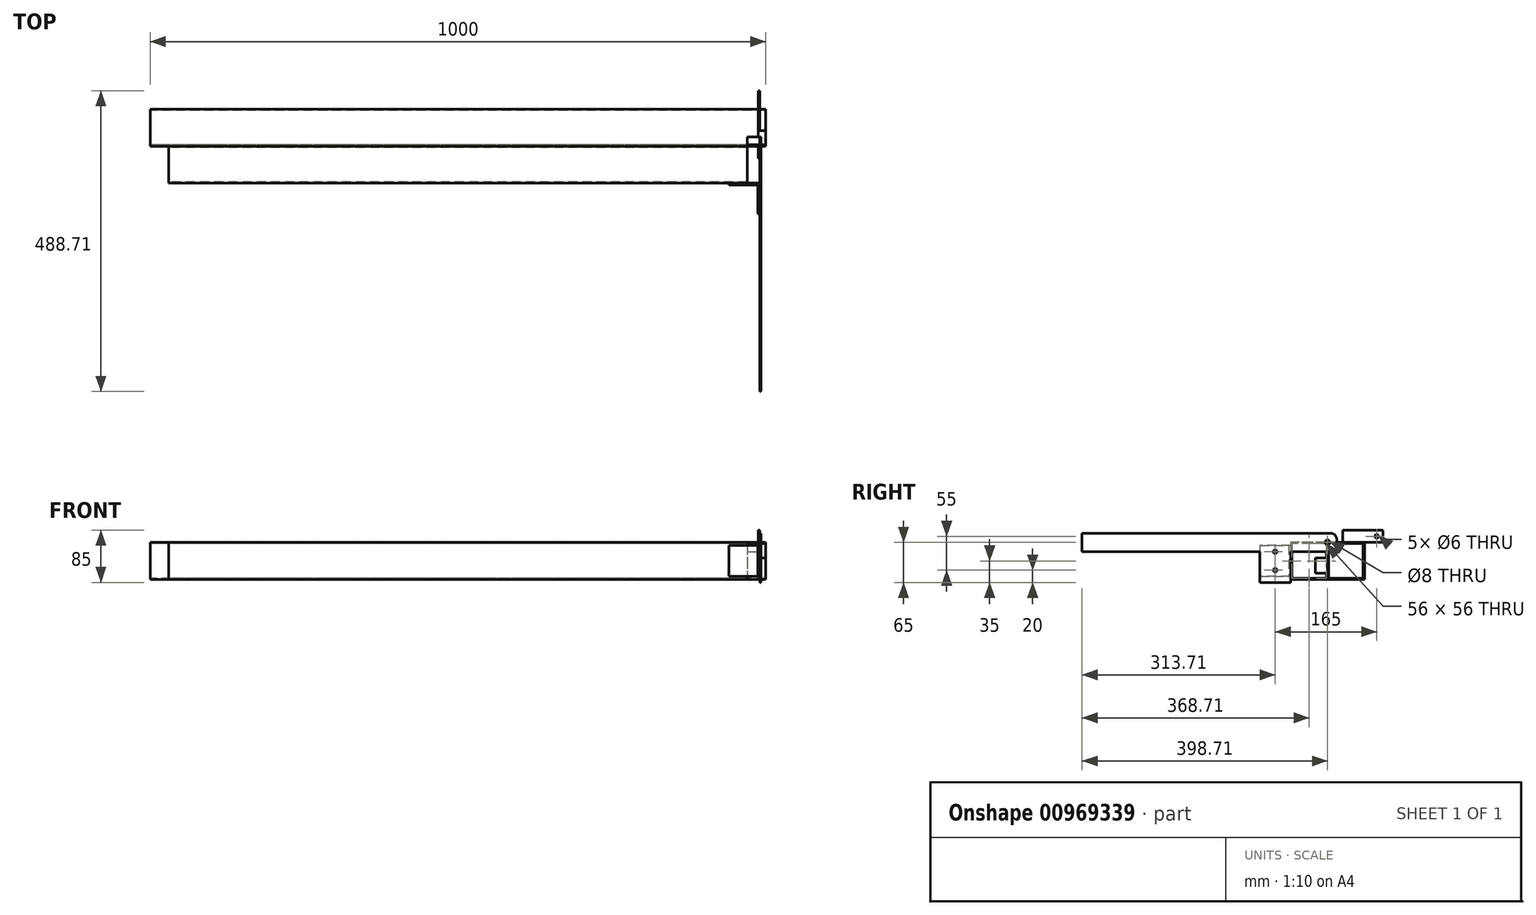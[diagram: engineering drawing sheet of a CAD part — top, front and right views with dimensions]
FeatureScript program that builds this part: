
annotation { "Feature Type Name" : "Feature", "Feature Type Description" : "" }
export const myFeature = defineFeature(function(context is Context, id is Id, definition is map)
    precondition{}
    {
        {
            var Q0;
            Q0=qCreatedBy(makeId("Right.planeOp"),FACE);
            var sketch = newSketch(context, id + "F0", { "sketchPlane" : qUnion([Q0])});
            skLineSegment(sketch, "E0.bottom", {"start": v(30, 30) * mm, "end": v(-30, 30) * mm});
            skLineSegment(sketch, "E0.top", {"start": v(30, -30) * mm, "end": v(-30, -30) * mm});
            skLineSegment(sketch, "E0.left", {"start": v(30, 30) * mm, "end": v(30, -30) * mm});
            skLineSegment(sketch, "E0.right", {"start": v(-30, 30) * mm, "end": v(-30, -30) * mm});
            skPoint(sketch, "E0.middle", {"position": v(0, 0) * mm});
            skLineSegment(sketch, "E1.bottom", {"start": v(28, 28) * mm, "end": v(-28, 28) * mm});
            skLineSegment(sketch, "E1.top", {"start": v(28, -28) * mm, "end": v(-28, -28) * mm});
            skLineSegment(sketch, "E1.left", {"start": v(28, 28) * mm, "end": v(28, -28) * mm});
            skLineSegment(sketch, "E1.right", {"start": v(-28, 28) * mm, "end": v(-28, -28) * mm});
            skSolve(sketch);
        }
        {
            var Q0;
            Q0=makeQuery(id+"F0.imprint","IMPRINT",FACE,{"disambiguationData":[TD([[makeQuery(id+"F0.imprint","IMPRINT",EDGE,{"derivedFrom":sQuery(id+"F0.wireOp",EDGE,"E0.bottom")}),1.0]])]});
            extrude(context, id + "F1", {"entities" : qUnion([Q0]), "depth" : 500 * mm, "offsetDistance" : 25 * mm, "hasSecondDirection" : true, "secondDirectionOppositeDirection" : true, "secondDirectionDepth" : 500 * mm});
        }
        {
            var Q0;
            Q0=qCreatedBy(makeId("Right.planeOp"),FACE);
            cPlane(context, id + "F2", {"entities" : qUnion([Q0]), "cplaneType" : CPlaneType.OFFSET, "offset" : 490 * mm, "width" : 150 * mm, "height" : 150 * mm});
        }
        {
            var Q0;
            Q0=qCreatedBy(id+"F2.planeOp",FACE);
            var sketch = newSketch(context, id + "F3", { "sketchPlane" : qUnion([Q0])});
            skLineSegment(sketch, "E2", {"start": v(-50, 50) * mm, "end": v(60, 50) * mm});
            skLineSegment(sketch, "E3", {"start": v(60, 50) * mm, "end": v(60, 30) * mm});
            skLineSegment(sketch, "E4", {"start": v(60, 30) * mm, "end": v(-10, 30) * mm});
            skLineSegment(sketch, "E5", {"start": v(-10, 30) * mm, "end": v(-10, 10) * mm});
            skLineSegment(sketch, "E6", {"start": v(-10, 10) * mm, "end": v(-30, 10) * mm});
            skLineSegment(sketch, "E7", {"start": v(-30, 10) * mm, "end": v(-30, -20) * mm});
            skLineSegment(sketch, "E8", {"start": v(-30, -20) * mm, "end": v(-50, -20) * mm});
            skLineSegment(sketch, "E9", {"start": v(-50, -20) * mm, "end": v(-50, 50) * mm});
            skCircle(sketch, "E10", {"center": v(-30, 30) * mm, "radius": 4 * mm});
            skCircle(sketch, "E11", {"center": v(50, 40) * mm, "radius": 3 * mm});
            skSolve(sketch);
        }
        {
            var Q0;
            Q0=makeQuery(id+"F3.imprint","IMPRINT",FACE,{"disambiguationData":[TD([[makeQuery(id+"F3.imprint","IMPRINT",EDGE,{"derivedFrom":sQuery(id+"F3.wireOp",EDGE,"E2")}),-1.0]])]});
            extrude(context, id + "F4", {"entities" : qUnion([Q0]), "oppositeDirection" : true, "depth" : 2 * mm, "offsetDistance" : 25 * mm});
        }
        {
            var Q0;
            Q0=makeQuery(id+"F1.opExtrude","CAP_FACE",FACE,{"disambiguationData":[OSD([sQuery(id+"F0.wireOp",EDGE,"E0.bottom"),sQuery(id+"F0.wireOp",EDGE,"E0.top"),sQuery(id+"F0.wireOp",EDGE,"E0.left"),sQuery(id+"F0.wireOp",EDGE,"E0.right"),sQuery(id+"F0.wireOp",EDGE,"E1.bottom"),sQuery(id+"F0.wireOp",EDGE,"E1.top"),sQuery(id+"F0.wireOp",EDGE,"E1.left"),sQuery(id+"F0.wireOp",EDGE,"E1.right")])],"isStart":false});
            cPlane(context, id + "F5", {"entities" : qUnion([Q0]), "cplaneType" : CPlaneType.OFFSET, "offset" : 30 * mm, "oppositeDirection" : true, "width" : 150 * mm, "height" : 150 * mm});
        }
        {
            var Q0;
            Q0=makeQuery(id+"F1.opExtrude","CAP_FACE",FACE,{"disambiguationData":[OSD([sQuery(id+"F0.wireOp",EDGE,"E0.bottom"),sQuery(id+"F0.wireOp",EDGE,"E0.top"),sQuery(id+"F0.wireOp",EDGE,"E0.left"),sQuery(id+"F0.wireOp",EDGE,"E0.right"),sQuery(id+"F0.wireOp",EDGE,"E1.bottom"),sQuery(id+"F0.wireOp",EDGE,"E1.top"),sQuery(id+"F0.wireOp",EDGE,"E1.left"),sQuery(id+"F0.wireOp",EDGE,"E1.right")])],"isStart":false});
            cPlane(context, id + "F6", {"entities" : qUnion([Q0]), "cplaneType" : CPlaneType.OFFSET, "offset" : 12 * mm, "oppositeDirection" : true, "width" : 150 * mm, "height" : 150 * mm});
        }
        {
            var Q0;
            Q0=qCreatedBy(id+"F5.planeOp",FACE);
            var sketch = newSketch(context, id + "F7", { "sketchPlane" : qUnion([Q0])});
            skLineSegment(sketch, "E12.bottom", {"start": v(-35.72, 35.11) * mm, "end": v(-15, 35.11) * mm});
            skLineSegment(sketch, "E12.top", {"start": v(-35.72, 15) * mm, "end": v(-15, 15) * mm});
            skLineSegment(sketch, "E12.left", {"start": v(-35.72, 35.11) * mm, "end": v(-35.72, 15) * mm});
            skLineSegment(sketch, "E12.right", {"start": v(-15, 35.11) * mm, "end": v(-15, 15) * mm});
            skSolve(sketch);
        }
        {
            var Q0;
            Q0=makeQuery(id+"F7.imprint","IMPRINT",FACE,{"disambiguationData":[TD([[makeQuery(id+"F7.imprint","IMPRINT",EDGE,{"derivedFrom":sQuery(id+"F7.wireOp",EDGE,"E12.bottom")}),-1.0]])]});
            extrude(context, id + "F8", {"entities" : qUnion([Q0]), "operationType" : NewBodyOperationType.REMOVE, "depth" : 100 * mm, "offsetDistance" : 25 * mm});
        }
        {
            var Q0;
            Q0=qCreatedBy(id+"F6.planeOp",FACE);
            var sketch = newSketch(context, id + "F9", { "sketchPlane" : qUnion([Q0])});
            skLineSegment(sketch, "E13.bottom", {"start": v(-60.98, 60.55) * mm, "end": v(-5, 60.55) * mm});
            skLineSegment(sketch, "E13.top", {"start": v(-60.98, 5) * mm, "end": v(-5, 5) * mm});
            skLineSegment(sketch, "E13.left", {"start": v(-60.98, 60.55) * mm, "end": v(-60.98, 5) * mm});
            skLineSegment(sketch, "E13.right", {"start": v(-5, 60.55) * mm, "end": v(-5, 5) * mm});
            skSolve(sketch);
        }
        {
            var Q0;
            Q0=makeQuery(id+"F9.imprint","IMPRINT",FACE,{"disambiguationData":[TD([[makeQuery(id+"F9.imprint","IMPRINT",EDGE,{"derivedFrom":sQuery(id+"F9.wireOp",EDGE,"E13.bottom")}),-1.0]])]});
            extrude(context, id + "F10", {"entities" : qUnion([Q0]), "operationType" : NewBodyOperationType.REMOVE, "depth" : 25 * mm, "offsetDistance" : 25 * mm});
        }
        {
            var Q0;
            Q0=qCreatedBy(makeId("Right.planeOp"),FACE);
            var sketch = newSketch(context, id + "F11", { "sketchPlane" : qUnion([Q0])});
            skLineSegment(sketch, "E14.bottom", {"start": v(-30, 30) * mm, "end": v(-90, 30) * mm});
            skLineSegment(sketch, "E14.top", {"start": v(-30, -30) * mm, "end": v(-90, -30) * mm});
            skLineSegment(sketch, "E14.left", {"start": v(-30, 30) * mm, "end": v(-30, -30) * mm});
            skLineSegment(sketch, "E14.right", {"start": v(-90, 30) * mm, "end": v(-90, -30) * mm});
            skLineSegment(sketch, "E15.bottom", {"start": v(-32, 28) * mm, "end": v(-88, 28) * mm});
            skLineSegment(sketch, "E15.top", {"start": v(-32, -28) * mm, "end": v(-88, -28) * mm});
            skLineSegment(sketch, "E15.left", {"start": v(-32, 28) * mm, "end": v(-32, -28) * mm});
            skLineSegment(sketch, "E15.right", {"start": v(-88, 28) * mm, "end": v(-88, -28) * mm});
            skSolve(sketch);
        }
        {
            var Q0;
            Q0=makeQuery(id+"F11.imprint","IMPRINT",FACE,{"disambiguationData":[TD([[makeQuery(id+"F11.imprint","IMPRINT",EDGE,{"derivedFrom":sQuery(id+"F11.wireOp",EDGE,"E14.bottom")}),1.0]])]});
            extrude(context, id + "F12", {"entities" : qUnion([Q0]), "depth" : 470 * mm, "offsetDistance" : 25 * mm, "hasSecondDirection" : true, "secondDirectionOppositeDirection" : true, "secondDirectionDepth" : 470 * mm});
        }
        {
            var Q0;
            Q0=qCreatedBy(id+"F2.planeOp",FACE);
            var sketch = newSketch(context, id + "F13", { "sketchPlane" : qUnion([Q0])});
            skLineSegment(sketch, "E16.bottom", {"start": v(-25, 45) * mm, "end": v(-428.7, 45) * mm});
            skLineSegment(sketch, "E16.top", {"start": v(-25, 15) * mm, "end": v(-90, 15) * mm});
            skLineSegment(sketch, "E16.left", {"start": v(-15, 35) * mm, "end": v(-15, 25) * mm});
            skLineSegment(sketch, "E16.right", {"start": v(-428.7, 45) * mm, "end": v(-428.7, 15) * mm});
            skPoint(sketch, "E17.visualSharp", {"position": v(-15, 45) * mm});
            skArc(sketch, "E17.filletArc", {"start": v(-15, 35) * mm, "mid": v(-17.93, 42.07) * mm, "end": v(-25, 45) * mm});
            skPoint(sketch, "E18.visualSharp", {"position": v(-15, 15) * mm});
            skArc(sketch, "E18.filletArc", {"start": v(-25, 15) * mm, "mid": v(-17.93, 17.93) * mm, "end": v(-15, 25) * mm});
            skCircle(sketch, "E19", {"center": v(-30, 30) * mm, "radius": 4 * mm});
            skLineSegment(sketch, "E20.top", {"start": v(-90, -35) * mm, "end": v(-140, -35) * mm});
            skLineSegment(sketch, "E20.left", {"start": v(-90, 15) * mm, "end": v(-90, -35) * mm});
            skLineSegment(sketch, "E20.right", {"start": v(-140, 15) * mm, "end": v(-140, -35) * mm});
            skLineSegment(sketch, "E21.trimOffspring", {"start": v(-140, 15) * mm, "end": v(-428.7, 15) * mm});
            skCircle(sketch, "E22", {"center": v(-115, -15) * mm, "radius": 3 * mm});
            skCircle(sketch, "E23", {"center": v(-115, 15) * mm, "radius": 3 * mm});
            skSolve(sketch);
        }
        {
            var Q0;
            Q0=makeQuery(id+"F13.imprint","IMPRINT",FACE,{"disambiguationData":[TD([[makeQuery(id+"F13.imprint","IMPRINT",EDGE,{"derivedFrom":sQuery(id+"F13.wireOp",EDGE,"E16.bottom")}),1.0]])]});
            extrude(context, id + "F14", {"entities" : qUnion([Q0]), "depth" : 2 * mm, "offsetDistance" : 25 * mm});
        }
        {
            var Q0;
            Q0=qCreatedBy(makeId("Top.planeOp"),FACE);
            var sketch = newSketch(context, id + "F15", { "sketchPlane" : qUnion([Q0])});
            skLineSegment(sketch, "E24", {"start": v(440, -90) * mm, "end": v(490, -90) * mm});
            skLineSegment(sketch, "E25", {"start": v(490, -90) * mm, "end": v(490, -140) * mm});
            skLineSegment(sketch, "E26", {"start": v(490, -140) * mm, "end": v(487, -140) * mm});
            skLineSegment(sketch, "E27", {"start": v(487, -140) * mm, "end": v(487, -93) * mm});
            skLineSegment(sketch, "E28", {"start": v(487, -93) * mm, "end": v(440, -93) * mm});
            skLineSegment(sketch, "E29", {"start": v(440, -93) * mm, "end": v(440, -90) * mm});
            skSolve(sketch);
        }
        {
            var Q0;
            Q0=makeQuery(id+"F15.imprint","IMPRINT",FACE,{"disambiguationData":[TD([[makeQuery(id+"F15.imprint","IMPRINT",EDGE,{"derivedFrom":sQuery(id+"F15.wireOp",EDGE,"E24")}),-1.0]])]});
            extrude(context, id + "F16", {"entities" : qUnion([Q0]), "endBound" : BoundingType.SYMMETRIC, "depth" : 50 * mm, "offsetDistance" : 25 * mm, "hasSecondDirection" : true, "secondDirectionOppositeDirection" : true, "secondDirectionDepth" : 25 * mm});
        }
        {
            var Q0;
            Q0=makeQuery(id+"F16.opExtrude","SWEPT_FACE",FACE,{"disambiguationData":[OSD([sQuery(id+"F15.wireOp",EDGE,"E27")])]});
            var sketch = newSketch(context, id + "F17", { "sketchPlane" : qUnion([Q0])});
            skPoint(sketch, "E30", {"position": v(115, 15) * mm});
            skPoint(sketch, "E31", {"position": v(115, -15) * mm});
            skSolve(sketch);
        }
        {
            var Q0;
            Q0=sQuery(id+"F17.wireOp",VERTEX,"E30");
            var Q1;
            Q1=makeQuery(id+"F16.opExtrude","SWEPT_BODY",BODY,{"disambiguationData":[OSD([sQuery(id+"F15.wireOp",EDGE,"E24"),sQuery(id+"F15.wireOp",EDGE,"E25"),sQuery(id+"F15.wireOp",EDGE,"E26"),sQuery(id+"F15.wireOp",EDGE,"E27"),sQuery(id+"F15.wireOp",EDGE,"E28"),sQuery(id+"F15.wireOp",EDGE,"E29")])]});
            hole(context, id + "F18", {"style" : HoleStyle.SIMPLE, "endStyle" : HoleEndStyle.THROUGH, "holeDiameter" : 6 * mm, "majorDiameter" : 5 * mm, "isTappedThrough" : true, "tappedDepth" : 12 * mm, "tapClearance" : 3, "locations" : qUnion([Q0]), "scope" : qUnion([Q1])});
        }
        {
            var Q0;
            Q0=makeQuery(id+"F16.opExtrude","SWEPT_FACE",FACE,{"disambiguationData":[OSD([sQuery(id+"F15.wireOp",EDGE,"E27")])]});
            var sketch = newSketch(context, id + "F19", { "sketchPlane" : qUnion([Q0])});
            skPoint(sketch, "E32", {"position": v(115, -15) * mm});
            skSolve(sketch);
        }
        {
            var Q0;
            Q0=sQuery(id+"F19.wireOp",VERTEX,"E32");
            var Q1;
            Q1=makeQuery(id+"F16.opExtrude","SWEPT_BODY",BODY,{"disambiguationData":[OSD([sQuery(id+"F15.wireOp",EDGE,"E24"),sQuery(id+"F15.wireOp",EDGE,"E25"),sQuery(id+"F15.wireOp",EDGE,"E26"),sQuery(id+"F15.wireOp",EDGE,"E27"),sQuery(id+"F15.wireOp",EDGE,"E28"),sQuery(id+"F15.wireOp",EDGE,"E29")])]});
            hole(context, id + "F20", {"style" : HoleStyle.SIMPLE, "endStyle" : HoleEndStyle.THROUGH, "holeDiameter" : 6 * mm, "majorDiameter" : 5 * mm, "isTappedThrough" : true, "tappedDepth" : 12 * mm, "tapClearance" : 3, "locations" : qUnion([Q0]), "scope" : qUnion([Q1])});
        }
    });
